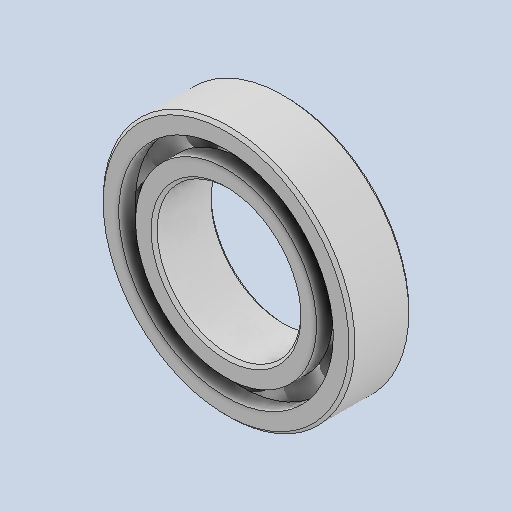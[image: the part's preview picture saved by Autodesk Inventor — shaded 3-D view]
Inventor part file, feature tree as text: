
AUTODESK INVENTOR PART (.ipt)
format: ipt  version: 2023 (Build 270158000, 158)  size: 578,048 bytes
history: native  units: in
note: dims shown in document units (in); Inventor stores cm internally (conversion verified against a paired STEP export)
features: other x11, revolve x3
ambient origin geometry x8: Origin, YZ Plane, XZ Plane, XY Plane, X Axis, Y Axis, Z Axis, Center Point
bodies: Solid1 (feature_tree), Solid2 (feature_tree), Solid3 (feature_tree), Solid4 (feature_tree), Solid5 (feature_tree), Solid6 (feature_tree), Solid7 (feature_tree), Solid8 (feature_tree), Solid9 (feature_tree), Solid10 (feature_tree), Solid11 (feature_tree), Solid12 (feature_tree), Solid13 (feature_tree), Solid14 (feature_tree)
feature tree (14):
  revolve  "Revolve1"  [1 undecoded]
  revolve  "Revolve3"  [1 undecoded]
  revolve  "Revolve4"  [1 undecoded]
  other  "CirPattern1[1]"
  other  "CirPattern1[2]"
  other  "CirPattern1[3]"
  other  "CirPattern1[4]"
  other  "CirPattern1[5]"
  other  "CirPattern1[6]"
  other  "CirPattern1[7]"
  other  "CirPattern1[8]"
  other  "CirPattern1[9]"
  other  "CirPattern1[10]"
  other  "CirPattern1[11]"
note: 3 required parameter values undecoded (feature->parameter linkage not recoverable at this tier; creation-order binding heuristic only, values carry confidence <= 0.55)
